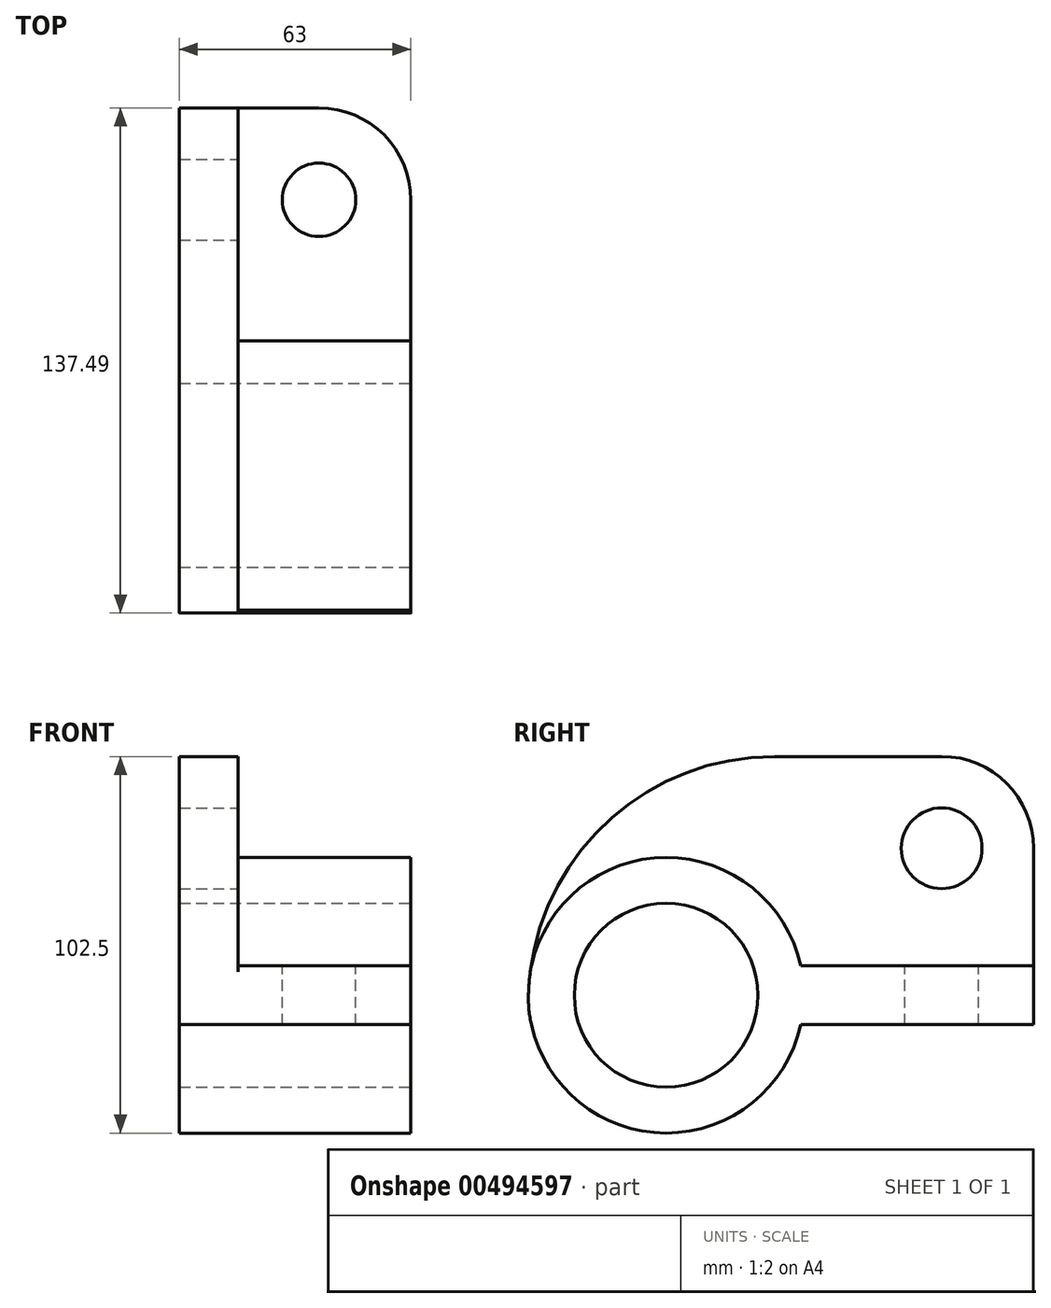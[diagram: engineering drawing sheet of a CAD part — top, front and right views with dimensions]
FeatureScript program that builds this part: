
annotation { "Feature Type Name" : "Feature", "Feature Type Description" : "" }
export const myFeature = defineFeature(function(context is Context, id is Id, definition is map)
    precondition{}
    {
        {
            var Q0;
            Q0=qCreatedBy(makeId("Right.planeOp"),FACE);
            var sketch = newSketch(context, id + "F0", { "sketchPlane" : qUnion([Q0])});
            skLineSegment(sketch, "E0", {"start": v(-73.56, 33.46) * mm, "end": v(63.94, 33.46) * mm});
            skLineSegment(sketch, "E1", {"start": v(-73.56, 33.46) * mm, "end": v(-73.56, -31.54) * mm});
            skLineSegment(sketch, "E2", {"start": v(63.94, 33.46) * mm, "end": v(63.94, -23.54) * mm});
            skLineSegment(sketch, "E3", {"start": v(63.94, -23.54) * mm, "end": v(63.94, -39.54) * mm});
            skLineSegment(sketch, "E4", {"start": v(63.94, -39.54) * mm, "end": v(-73.56, -39.54) * mm});
            skLineSegment(sketch, "E5", {"start": v(-73.56, -39.54) * mm, "end": v(-73.56, -31.54) * mm});
            skSolve(sketch);
        }
        {
            var Q0;
            Q0 = qSketchRegion(id + "F0", true);
            extrude(context, id + "F1", {"entities" : qUnion([Q0]), "depth" : 16 * mm});
        }
        {
            var Q0;
            Q0=makeQuery(id+"F1.opExtrude","CAP_FACE",FACE,{"disambiguationData":[OSD([sQuery(id+"F0.wireOp",EDGE,"E0"),sQuery(id+"F0.wireOp",EDGE,"E1"),sQuery(id+"F0.wireOp",EDGE,"E2"),sQuery(id+"F0.wireOp",EDGE,"E3"),sQuery(id+"F0.wireOp",EDGE,"E4"),sQuery(id+"F0.wireOp",EDGE,"E5")])],"isStart":false});
            var sketch = newSketch(context, id + "F2", { "sketchPlane" : qUnion([Q0])});
            skLineSegment(sketch, "E6", {"start": v(63.94, -39.54) * mm, "end": v(63.94, -23.54) * mm});
            skLineSegment(sketch, "E7", {"start": v(63.94, -23.54) * mm, "end": v(-73.56, -23.54) * mm});
            skLineSegment(sketch, "E8", {"start": v(-73.56, -23.54) * mm, "end": v(-73.56, -39.54) * mm});
            skLineSegment(sketch, "E9", {"start": v(-73.56, -39.54) * mm, "end": v(63.94, -39.54) * mm});
            skSolve(sketch);
        }
        {
            var Q0;
            Q0=makeQuery(id+"F2.imprint","IMPRINT",FACE,{"disambiguationData":[TD([[makeQuery(id+"F2.imprint","IMPRINT",EDGE,{"derivedFrom":sQuery(id+"F2.wireOp",EDGE,"E6")}),-1.0]])]});
            extrude(context, id + "F3", {"entities" : qUnion([Q0]), "operationType" : NewBodyOperationType.ADD, "depth" : 47 * mm});
        }
        {
            var Q0;
            Q0=makeQuery(id+"F3.opExtrude","CAP_FACE",FACE,{"disambiguationData":[OSD([sQuery(id+"F2.wireOp",EDGE,"E6"),sQuery(id+"F2.wireOp",EDGE,"E7"),sQuery(id+"F2.wireOp",EDGE,"E8"),sQuery(id+"F2.wireOp",EDGE,"E9")])],"isStart":false});
            var sketch = newSketch(context, id + "F4", { "sketchPlane" : qUnion([Q0])});
            skLineSegment(sketch, "E10", {"start": v(-73.56, -31.54) * mm, "end": v(-36.06, -31.54) * mm});
            skCircle(sketch, "E11", {"center": v(-36.06, -31.54) * mm, "radius": 37.5 * mm});
            skSolve(sketch);
        }
        {
            var Q0;
            Q0 = qSketchRegion(id + "F4", true);
            extrude(context, id + "F5", {"entities" : qUnion([Q0]), "operationType" : NewBodyOperationType.ADD, "oppositeDirection" : true, "depth" : 63 * mm});
        }
        {
            var Q0;
            Q0=makeQuery(id+"F1.opExtrude","CAP_FACE",FACE,{"disambiguationData":[OSD([sQuery(id+"F0.wireOp",EDGE,"E0"),sQuery(id+"F0.wireOp",EDGE,"E1"),sQuery(id+"F0.wireOp",EDGE,"E2"),sQuery(id+"F0.wireOp",EDGE,"E3"),sQuery(id+"F0.wireOp",EDGE,"E4"),sQuery(id+"F0.wireOp",EDGE,"E5")])],"isStart":false});
            var sketch = newSketch(context, id + "F6", { "sketchPlane" : qUnion([Q0])});
            skLineSegment(sketch, "E12", {"start": v(-36.06, 5.96) * mm, "end": v(-36.06, 8.46) * mm});
            skLineSegment(sketch, "E13", {"start": v(-36.06, 8.46) * mm, "end": v(38.94, 8.46) * mm});
            skCircle(sketch, "E14", {"center": v(38.94, 8.46) * mm, "radius": 11 * mm});
            skSolve(sketch);
        }
        {
            var Q0;
            Q0 = qSketchRegion(id + "F6", true);
            extrude(context, id + "F7", {"entities" : qUnion([Q0]), "operationType" : NewBodyOperationType.REMOVE, "oppositeDirection" : true, "depth" : 25 * mm});
        }
        {
            var Q0;
            Q0=makeQuery(id+"F1.opExtrude","SWEPT_EDGE",EDGE,{"disambiguationData":[OSD([sQuery(id+"F0.wireOp",EDGE,"E0"),sQuery(id+"F0.wireOp",EDGE,"E2")])]});
            var Q1;
            Q1=makeQuery(id+"F3.opExtrude","CAP_EDGE",EDGE,{"disambiguationData":[OSD([sQuery(id+"F2.wireOp",EDGE,"E6")])],"isStart":false});
            fillet(context, id + "F8", {"entities" : qUnion([Q0, Q1]), "radius" : 25 * mm, "tangentPropagation" : true, "allowEdgeOverflow" : false});
        }
        {
            var Q0;
            {var subQ0=sQuery(id+"F2.wireOp",EDGE,"E7");var subQ1=sQuery(id+"F2.wireOp",EDGE,"E6");Q0=makeQuery(id+"F5.boolean.opBoolean","SPLIT",FACE,{"disambiguationData":[TD([makeQuery(id+"F3.opExtrude","SWEPT_FACE",FACE,{"disambiguationData":[OSD([subQ1])]})])],"derivedFrom":makeQuery(id+"F3.opExtrude","SWEPT_FACE",FACE,{"disambiguationData":[OSD([subQ0])]})});}
            var sketch = newSketch(context, id + "F9", { "sketchPlane" : qUnion([Q0])});
            skLineSegment(sketch, "E15", {"start": v(55.68, 56.61) * mm, "end": v(38, 38.94) * mm});
            skCircle(sketch, "E16", {"center": v(38, 38.94) * mm, "radius": 10 * mm});
            skSolve(sketch);
        }
        {
            var Q0;
            Q0 = qSketchRegion(id + "F9", true);
            extrude(context, id + "F10", {"entities" : qUnion([Q0]), "operationType" : NewBodyOperationType.REMOVE, "oppositeDirection" : true, "depth" : 25 * mm});
        }
        {
            var Q0;
            Q0=makeQuery(id+"F5.boolean.opBoolean","MERGE",FACE,{"derivedFrom":[makeQuery(id+"F3.opExtrude","CAP_FACE",FACE,{"disambiguationData":[OSD([sQuery(id+"F2.wireOp",EDGE,"E6"),sQuery(id+"F2.wireOp",EDGE,"E7"),sQuery(id+"F2.wireOp",EDGE,"E8"),sQuery(id+"F2.wireOp",EDGE,"E9")])],"isStart":false}),makeQuery(id+"F5.opExtrude","CAP_FACE",FACE,{"disambiguationData":[OSD([sQuery(id+"F4.wireOp",EDGE,"E11")])],"isStart":true})]});
            var sketch = newSketch(context, id + "F11", { "sketchPlane" : qUnion([Q0])});
            skCircle(sketch, "E17", {"center": v(-36.06, -31.54) * mm, "radius": 25 * mm});
            skSolve(sketch);
        }
        {
            var Q0;
            Q0 = qSketchRegion(id + "F11", true);
            extrude(context, id + "F12", {"entities" : qUnion([Q0]), "operationType" : NewBodyOperationType.REMOVE, "oppositeDirection" : true, "depth" : 500 * mm});
        }
        {
            var Q0;
            Q0=makeQuery(id+"F1.opExtrude","SWEPT_EDGE",EDGE,{"disambiguationData":[OSD([sQuery(id+"F0.wireOp",EDGE,"E0"),sQuery(id+"F0.wireOp",EDGE,"E1")])]});
            fillet(context, id + "F13", {"entities" : qUnion([Q0]), "radius" : 67 * mm, "tangentPropagation" : true, "allowEdgeOverflow" : false});
        }
        {
            var Q0;
            Q0=makeQuery(id+"F3.boolean.opBoolean","MERGE",EDGE,{"derivedFrom":[makeQuery(id+"F1.opExtrude","SWEPT_EDGE",EDGE,{"disambiguationData":[OSD([sQuery(id+"F0.wireOp",EDGE,"E4"),sQuery(id+"F0.wireOp",EDGE,"E5")])]}),makeQuery(id+"F3.opExtrude","SWEPT_EDGE",EDGE,{"disambiguationData":[OSD([sQuery(id+"F2.wireOp",EDGE,"E8"),sQuery(id+"F2.wireOp",EDGE,"E9")])]})]});
            fillet(context, id + "F14", {"entities" : qUnion([Q0]), "radius" : 30 * mm, "tangentPropagation" : true, "allowEdgeOverflow" : false});
        }
        {
            var Q0;
            {var subQ0=sQuery(id+"F2.wireOp",EDGE,"E8");var subQ1=sQuery(id+"F2.wireOp",EDGE,"E7");var subQ3=sQuery(id+"F0.wireOp",EDGE,"E1");var subQ4=sQuery(id+"F0.wireOp",EDGE,"E0");Q0=makeQuery(id+"F13.opFillet","BLEND_EDGE",EDGE,{"blendedFrom":[makeQuery(id+"F1.opExtrude","SWEPT_EDGE",EDGE,{"disambiguationData":[OSD([subQ4,subQ3])]}),makeQuery(id+"F5.boolean.opBoolean","SPLIT",FACE,{"disambiguationData":[TD([makeQuery(id+"F3.opExtrude","SWEPT_FACE",FACE,{"disambiguationData":[OSD([subQ0])]})])],"derivedFrom":makeQuery(id+"F3.opExtrude","SWEPT_FACE",FACE,{"disambiguationData":[OSD([subQ1])]})})],"blendedInto":[makeQuery(id+"F5.boolean.opBoolean","SPLIT",FACE,{"disambiguationData":[TD([makeQuery(id+"F3.opExtrude","SWEPT_FACE",FACE,{"disambiguationData":[OSD([subQ0])]})])],"derivedFrom":makeQuery(id+"F3.opExtrude","SWEPT_FACE",FACE,{"disambiguationData":[OSD([subQ1])]})})]});}
            fillet(context, id + "F15", {"entities" : qUnion([Q0]), "radius" : 10 * mm, "tangentPropagation" : true, "allowEdgeOverflow" : false});
        }
    });
